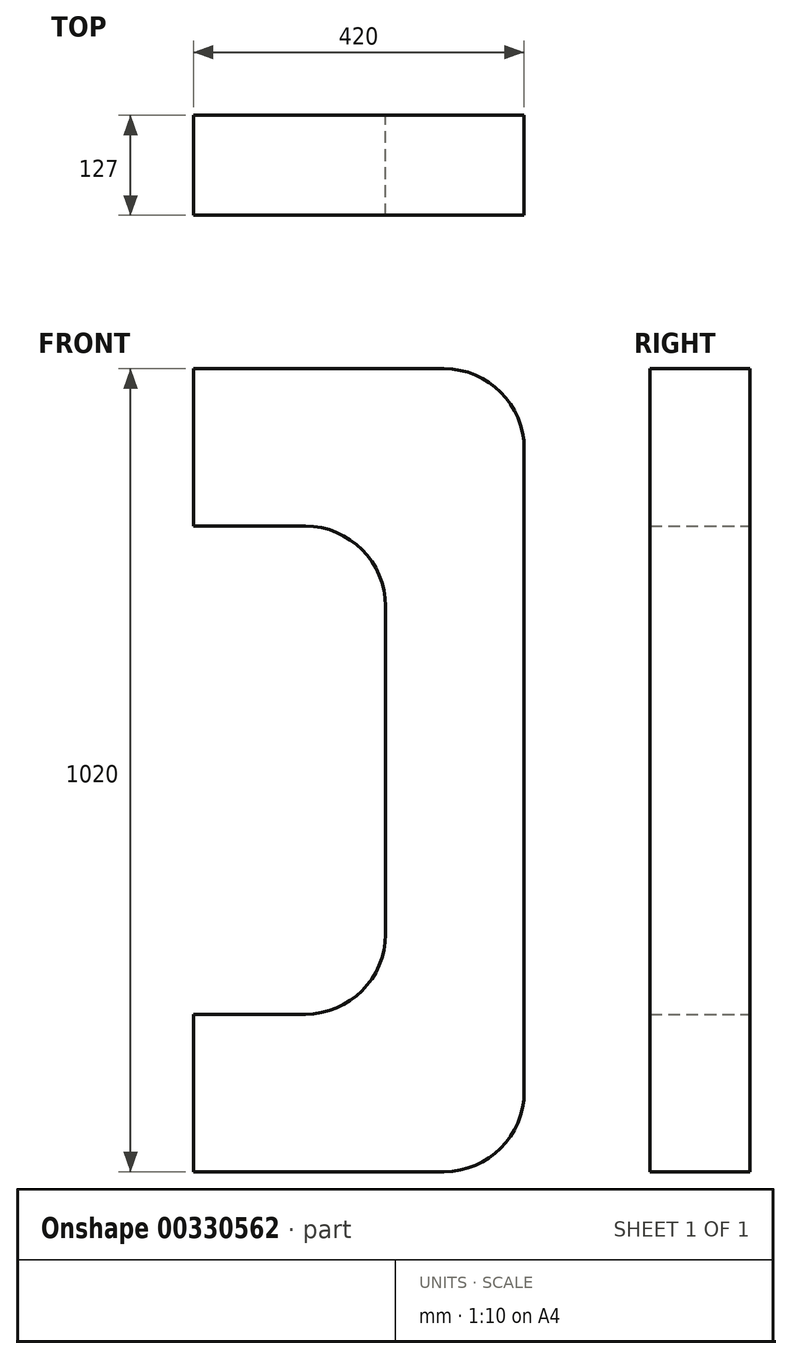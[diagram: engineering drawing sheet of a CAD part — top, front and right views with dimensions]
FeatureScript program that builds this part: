
annotation { "Feature Type Name" : "Feature", "Feature Type Description" : "" }
export const myFeature = defineFeature(function(context is Context, id is Id, definition is map)
    precondition{}
    {
        {
            var Q0;
            Q0=qCreatedBy(makeId("Front.planeOp"),FACE);
            var sketch = newSketch(context, id + "F0", { "sketchPlane" : qUnion([Q0])});
            skLineSegment(sketch, "E0.bottom", {"start": v(108.4, 510) * mm, "end": v(-210, 510) * mm});
            skLineSegment(sketch, "E0.top", {"start": v(108.4, -510) * mm, "end": v(-210, -510) * mm});
            skLineSegment(sketch, "E0.left", {"start": v(210, 408.4) * mm, "end": v(210, -408.4) * mm});
            skLineSegment(sketch, "E0.right", {"start": v(-210, 510) * mm, "end": v(-210, 310) * mm});
            skPoint(sketch, "E0.middle", {"position": v(0, 0) * mm});
            skLineSegment(sketch, "E1", {"start": v(-210, -510) * mm, "end": v(-210, -310) * mm});
            skLineSegment(sketch, "E2.trimOffspring", {"start": v(-210, -310) * mm, "end": v(-210, -510) * mm});
            skLineSegment(sketch, "E3", {"start": v(-210, 310) * mm, "end": v(-67.76, 310) * mm});
            skLineSegment(sketch, "E4", {"start": v(-210, -310) * mm, "end": v(-67.76, -310) * mm});
            skLineSegment(sketch, "E5", {"start": v(33.84, 208.4) * mm, "end": v(33.84, -208.4) * mm});
            skPoint(sketch, "E6.visualSharp", {"position": v(33.84, 310) * mm});
            skArc(sketch, "E6.filletArc", {"start": v(33.84, 208.4) * mm, "mid": v(4.08, 280.24) * mm, "end": v(-67.76, 310) * mm});
            skPoint(sketch, "E7.visualSharp", {"position": v(33.84, -310) * mm});
            skArc(sketch, "E7.filletArc", {"start": v(-67.76, -310) * mm, "mid": v(4.08, -280.24) * mm, "end": v(33.84, -208.4) * mm});
            skPoint(sketch, "E8.visualSharp", {"position": v(210, 510) * mm});
            skArc(sketch, "E8.filletArc", {"start": v(210, 408.4) * mm, "mid": v(180.24, 480.24) * mm, "end": v(108.4, 510) * mm});
            skPoint(sketch, "E9.visualSharp", {"position": v(210, -510) * mm});
            skArc(sketch, "E9.filletArc", {"start": v(108.4, -510) * mm, "mid": v(180.24, -480.24) * mm, "end": v(210, -408.4) * mm});
            skSolve(sketch);
        }
        {
            var Q0;
            Q0=makeQuery(id+"F0.imprint","IMPRINT",FACE,{"disambiguationData":[TD([[makeQuery(id+"F0.imprint","IMPRINT",EDGE,{"derivedFrom":sQuery(id+"F0.wireOp",EDGE,"E0.bottom")}),1.0]])]});
            extrude(context, id + "F1", {"entities" : qUnion([Q0]), "depth" : 127 * mm});
        }
    });
